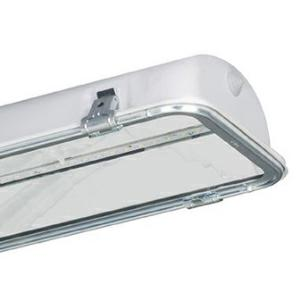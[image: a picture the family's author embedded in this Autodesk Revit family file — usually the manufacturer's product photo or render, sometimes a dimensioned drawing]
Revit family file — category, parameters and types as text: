
# Revit family: 3f_filippi_-_beta_i3f_76_vt_ampio_3f_filippi_-_55083_-_i3f_led_762x30w_ep_ampio_vt_l1565
name_source: partatom
category: Lighting Fixtures
units: mm (PartAtom-declared; Revit-internal decimal feet)

## family parameters
Cut with Voids When Loaded = No
Host = Face
Light Source = No
Part Type = Normal
Room Calculation Point = No
Round Connector Dimension = Use Diameter
Shared = No

## types (1)
- 3F Filippi - Beta i3F 76 VT Ampio (1 x LED, 9769 lm, 67 W, 4000 K)
    Apparent Load = 67 VA
    Approval mark = ENEC
    CIE Flux Codes = 52 86 99 100 100
    Color Rendering = 80
    Color Temperature = 4000 K
    Control Gear = Electronic ballast
    Default Elevation = 1800 mm
    Description = ILLUMINOTECHNICAL
Luminous efficiency 100% (DLOR 100%, ULOR 0%).
Initial luminous flux of the luminaire 9769 lm.
Emergency luminaire luminous flux BLF 5.7%.
Wide symmetric distribution.
Installation Interdistance Transv.D = 1.47 x hu - Long.D = 1.27 x hu.
Tabular UGR (CIE 117 - 4H-8H; S=0.25H; 70/50/20): RUG 21.3 - 24.6.
Beam angle: 101° - 108°.
Luminous efficacy 146 lm/W.
Lifetime (L93/B10): 30000 h. (tq+25°C)
Lifetime (L90/B10): 50000 h. (tq+25°C)
Lifetime (L85/B10): 80000 h. (tq+25°C)
Lifetime (L80/B10): 100000 h. (tq+25°C)
Sudden decreased luminous flux after 50000 hours: 0% (C0).
Photobiological safety in compliance with IEC/TR 62778: RG0 risk exempt, (IEC 62471).
In compliance with IEC/EN 62722-2-1 - IEC/EN 62717 standards.

SOURCE
2 linear LED modules 30W/840.
Energy efficiency class (UE 2019/2020 - UE 2019/2015): D.
CIE 13.3 Colour rendering index: CRI >80 (R9 <50%).
IES TM-30 Fidelity Index: Rf = 84 Rg = 95.
CCT nominal colour temperature 4000 K.
Colour initial tolerance (MacAdam): SDCM 3.

MECHANICAL
Single-piece housing in pressed steel, powder-coated in white epoxy-polyester.
Transparent glass, non-combustible, tempered, mounted and locked to the single-piece galvanised steel perimetrical frame, sealing gasket, hinged opening by means of galvanised steel clips.
Wide flow recuperator, oversized, in specular aluminium with superficial titanium-magnesium treatment, non-iridescent.
Gear-tray unit in hot-galvanised steel, painted in white polyester, fixed to the housing by means of "Ribloc" rapid devices in galvanised steel, hinged opening.
Luminaire with limited surface temperature. - D - (EN 60598-2-24)
Dimensions: 1565x235 mm, height 105 mm. Weight 10.565 kg.
IP65 protection degree.
Mechanical strength to impacts IK09 (10 joule).
Glow-wire test resistance 960°C.

ELECTRICAL
Halogen Free electronic wiring 230V-50/60Hz, power factor 0.95, THD <25%, constant output current, SELV, class I, 1 driver.
Power of the luminaire 67 W.
CE - IEC 60598-1 - EN 60598-1.
EP maintained emergency wiring on board, 1h duration, 24h recharge; compliant with EN 60598-2-22, excluding high risk areas.
SAFE FLICKER: PstLM=<1 and SVM=<0.4 (IEC TR 61547-1 and IEC TR 63158), to ensure a more comfortable and safe light.
Ambient temperature from +5°C to +25°C.
Temperature class T6 max 85°C.
Relative humidity UR: <85%.

INSTALLATION
Ceiling / Suspended / Wall.
All accessories dedicated to this product are available on the Catalog and on our website www.3F-Filippi.com.

APPLICATIONS
In industrial environments, stores and dry, dusty indoor environments, subject to occasional water splashes.

WARNING
Fixture not suitable for cold stores with an ambient temperature <5°C and/or relative humidity >85%.
Luminaire designed for disposal/recycling at end-of-life.
Replaceable (LED only) light source by a professional. Replaceable control gear by a professional.
    Height = 105 mm
    Lamp = 1 x LED
    Lamp Light Flux = 9769 lm
    Lamp Power = 67 W
    Lamp count = 1
    Length = 1565 mm
    Lifetime = 50000 h
    Luminous efficacy = 146 lm/W
    Manufacturer = 3F Filippi
    ModVariant = No
    Model = 3F Filippi - 55083 - i3F LED 762x30W EP AMPIO VT L1565
    Mounting Place = Ceiling
    Mounting Type = Pendant
    Number of Poles = 1
    OnlyDefault = Yes
    Power Factor = 1
    Product Name = 3F Filippi - Beta i3F 76 VT Ampio
    Product group = pendant luminaire
    ProductGroupID = 9
    Protection Class = Protection class I
    Protection Degree = IP 65
    RLX_Detail_Level = 1
    RLX_Emergency_Light_Flux = 0 lm
    RLX_Emergency_Type = 0
    RLX_Emergency_Type_DB = No
    RlxData = <blob elided: 69949 chars, md5=214c18ce>
    Socket = socket
    Standby Power = 0 W
    System Light Flux = 9769 lm
    System Power = 67 W
    Type Comments = Product without accessories
    Type Image = 3ffilippi_55083.jpg
    URL = http://relux.com
    VarID = ---
    Voltage = 0 V
    Weight = 0.00 kg
    Width = 235 mm

## geometry (parser evidence)
native form markers: Blend x4, Sweep x9
no freeform markers — native parametric forms only
